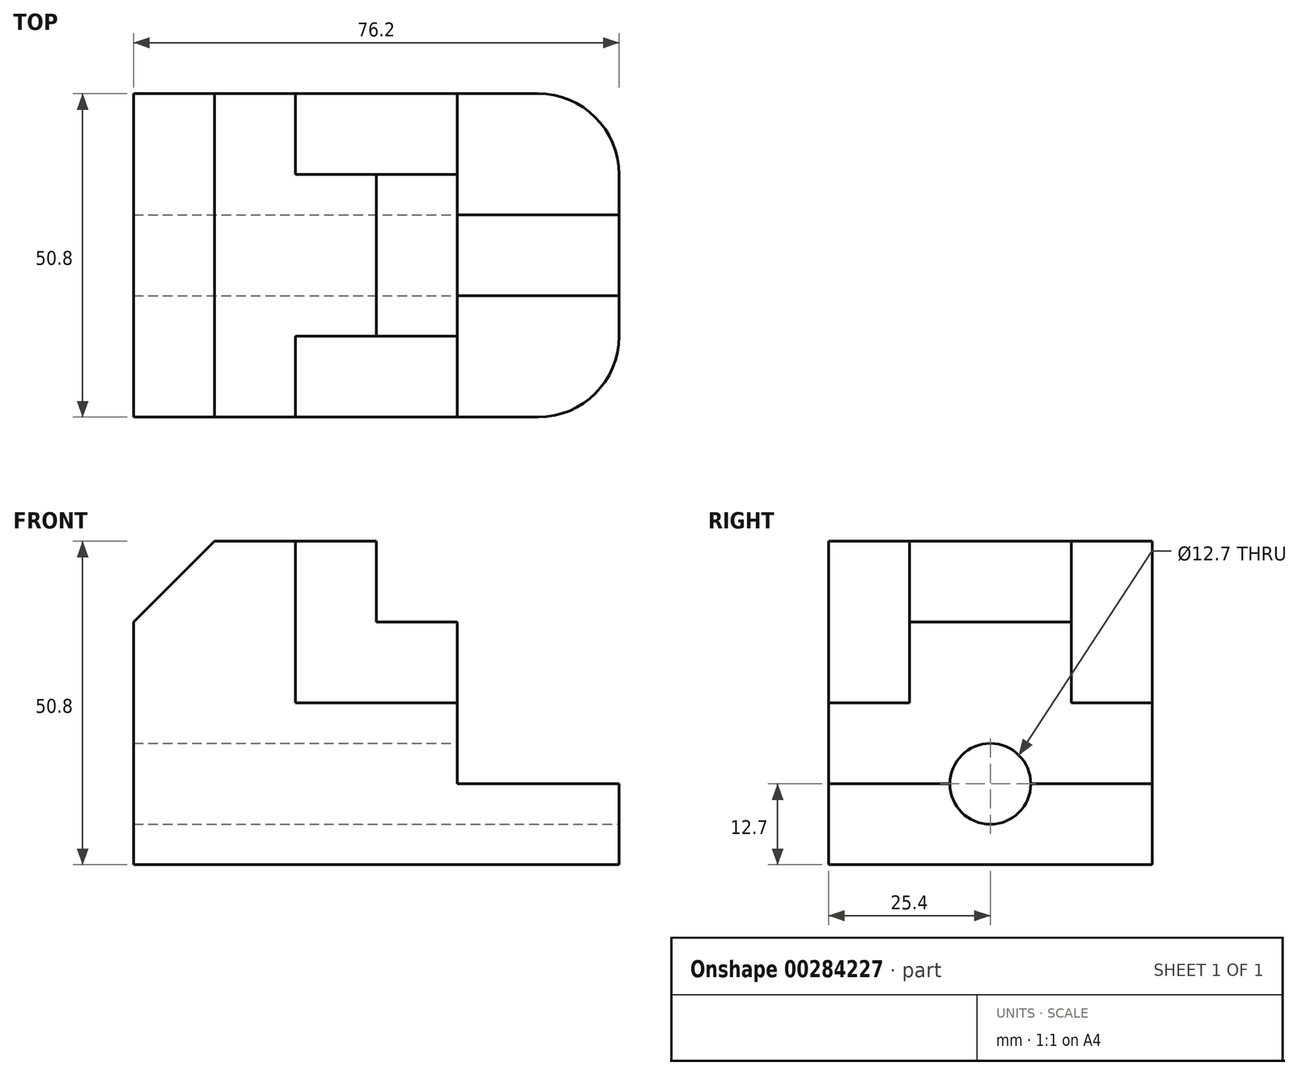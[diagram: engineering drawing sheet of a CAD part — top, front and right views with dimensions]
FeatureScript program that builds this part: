
annotation { "Feature Type Name" : "Feature", "Feature Type Description" : "" }
export const myFeature = defineFeature(function(context is Context, id is Id, definition is map)
    precondition{}
    {
        {
            var Q0;
            Q0=qCreatedBy(makeId("Front.planeOp"),FACE);
            var sketch = newSketch(context, id + "F0", { "sketchPlane" : qUnion([Q0])});
            skLineSegment(sketch, "E0", {"start": v(0, 0) * mm, "end": v(0, 38.1) * mm});
            skLineSegment(sketch, "E1", {"start": v(0, 38.1) * mm, "end": v(12.7, 50.8) * mm});
            skLineSegment(sketch, "E2", {"start": v(12.7, 50.8) * mm, "end": v(38.1, 50.8) * mm});
            skLineSegment(sketch, "E3", {"start": v(38.1, 50.8) * mm, "end": v(38.1, 38.1) * mm});
            skLineSegment(sketch, "E4", {"start": v(38.1, 38.1) * mm, "end": v(50.8, 38.1) * mm});
            skLineSegment(sketch, "E5", {"start": v(50.8, 38.1) * mm, "end": v(50.8, 12.7) * mm});
            skLineSegment(sketch, "E6", {"start": v(50.8, 12.7) * mm, "end": v(76.2, 12.7) * mm});
            skLineSegment(sketch, "E7", {"start": v(76.2, 12.7) * mm, "end": v(76.2, 0) * mm});
            skLineSegment(sketch, "E8", {"start": v(76.2, 0) * mm, "end": v(0, 0) * mm});
            skLineSegment(sketch, "E9", {"start": v(25.4, 50.8) * mm, "end": v(25.4, 25.4) * mm});
            skLineSegment(sketch, "E10", {"start": v(25.4, 25.4) * mm, "end": v(50.8, 25.4) * mm});
            skSolve(sketch);
        }
        {
            var Q0;
            Q0 = qSketchRegion(id + "F0", true);
            extrude(context, id + "F1", {"entities" : qUnion([Q0]), "endBound" : BoundingType.SYMMETRIC, "depth" : 50.8 * mm});
        }
        {
            var Q0;
            Q0=makeQuery(id+"F1.opExtrude","SWEPT_FACE",FACE,{"disambiguationData":[OSD([sQuery(id+"F0.wireOp",EDGE,"E2")])]});
            var sketch = newSketch(context, id + "F2", { "sketchPlane" : qUnion([Q0])});
            skLineSegment(sketch, "E11.bottom", {"start": v(25.4, 25.4) * mm, "end": v(50.8, 25.4) * mm});
            skLineSegment(sketch, "E11.top", {"start": v(25.4, 12.7) * mm, "end": v(50.8, 12.7) * mm});
            skLineSegment(sketch, "E11.left", {"start": v(25.4, 25.4) * mm, "end": v(25.4, 12.7) * mm});
            skLineSegment(sketch, "E11.right", {"start": v(50.8, 25.4) * mm, "end": v(50.8, 12.7) * mm});
            skLineSegment(sketch, "E12.bottom", {"start": v(25.4, -25.4) * mm, "end": v(50.8, -25.4) * mm});
            skLineSegment(sketch, "E12.top", {"start": v(25.4, -12.7) * mm, "end": v(50.8, -12.7) * mm});
            skLineSegment(sketch, "E12.left", {"start": v(25.4, -25.4) * mm, "end": v(25.4, -12.7) * mm});
            skLineSegment(sketch, "E12.right", {"start": v(50.8, -25.4) * mm, "end": v(50.8, -12.7) * mm});
            skSolve(sketch);
        }
        {
            var Q0;
            Q0 = qSketchRegion(id + "F2", true);
            extrude(context, id + "F3", {"entities" : qUnion([Q0]), "operationType" : NewBodyOperationType.REMOVE, "oppositeDirection" : true, "depth" : 25.4 * mm});
        }
        {
            var Q0;
            Q0=makeQuery(id+"F1.opExtrude","SWEPT_FACE",FACE,{"disambiguationData":[OSD([sQuery(id+"F0.wireOp",EDGE,"E7")])]});
            var sketch = newSketch(context, id + "F4", { "sketchPlane" : qUnion([Q0])});
            skCircle(sketch, "E13", {"center": v(0, 12.7) * mm, "radius": 6.35 * mm});
            skSolve(sketch);
        }
        {
            var Q0;
            Q0 = qSketchRegion(id + "F4", true);
            extrude(context, id + "F5", {"entities" : qUnion([Q0]), "operationType" : NewBodyOperationType.REMOVE, "endBound" : BoundingType.THROUGH_ALL, "oppositeDirection" : true, "depth" : 25.4 * mm});
        }
        {
            var Q0;
            Q0=makeQuery(id+"F1.opExtrude","CAP_EDGE",EDGE,{"disambiguationData":[OSD([sQuery(id+"F0.wireOp",EDGE,"E7")])],"isStart":false});
            var Q1;
            Q1=makeQuery(id+"F1.opExtrude","CAP_EDGE",EDGE,{"disambiguationData":[OSD([sQuery(id+"F0.wireOp",EDGE,"E7")])],"isStart":true});
            fillet(context, id + "F6", {"entities" : qUnion([Q0, Q1]), "radius" : 12.7 * mm, "tangentPropagation" : true, "allowEdgeOverflow" : false});
        }
    });
